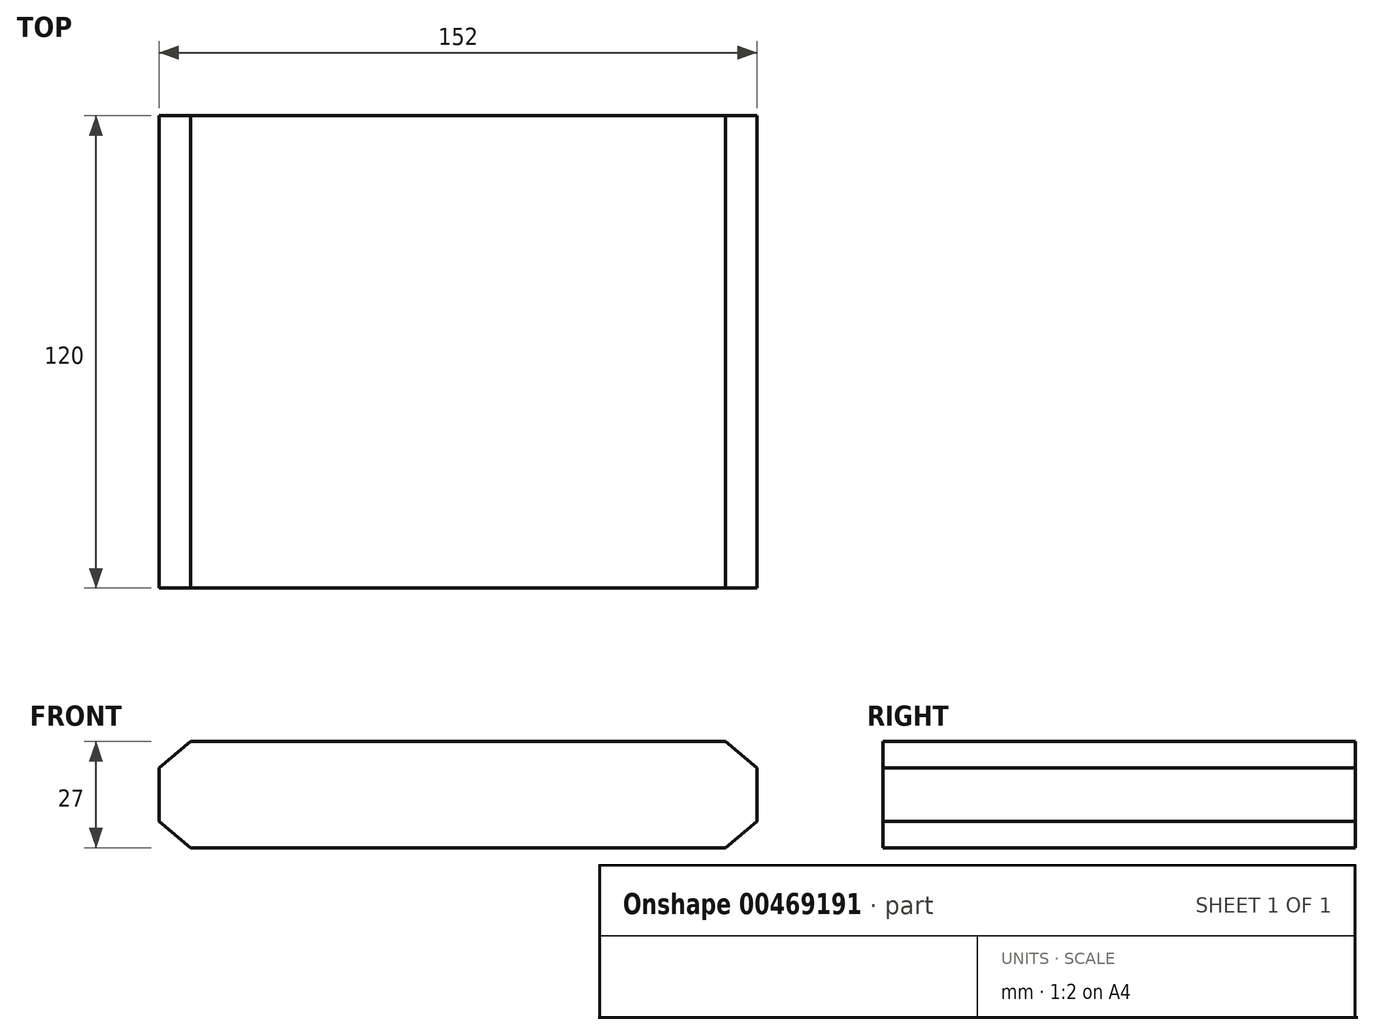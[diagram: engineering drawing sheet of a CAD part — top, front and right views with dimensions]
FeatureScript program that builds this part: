
annotation { "Feature Type Name" : "Feature", "Feature Type Description" : "" }
export const myFeature = defineFeature(function(context is Context, id is Id, definition is map)
    precondition{}
    {
        {
            var Q0;
            Q0=qCreatedBy(makeId("Top.planeOp"),FACE);
            var sketch = newSketch(context, id + "F0", { "sketchPlane" : qUnion([Q0])});
            skLineSegment(sketch, "E0.bottom", {"start": v(76, -60) * mm, "end": v(-76, -60) * mm});
            skLineSegment(sketch, "E0.top", {"start": v(76, 60) * mm, "end": v(-76, 60) * mm});
            skLineSegment(sketch, "E0.left", {"start": v(76, -60) * mm, "end": v(76, 60) * mm});
            skLineSegment(sketch, "E0.right", {"start": v(-76, -60) * mm, "end": v(-76, 60) * mm});
            skPoint(sketch, "E0.middle", {"position": v(0, 0) * mm});
            skSolve(sketch);
        }
        {
            var Q0;
            Q0 = qSketchRegion(id + "F0", true);
            extrude(context, id + "F1", {"entities" : qUnion([Q0]), "depth" : 27 * mm});
        }
        {
            var Q0;
            Q0=makeQuery(id+"F1.opExtrude","SWEPT_FACE",FACE,{"disambiguationData":[OSD([sQuery(id+"F0.wireOp",EDGE,"E0.top")])]});
            var sketch = newSketch(context, id + "F2", { "sketchPlane" : qUnion([Q0])});
            skLineSegment(sketch, "E1.bottom", {"start": v(60, 0) * mm, "end": v(-60, 0) * mm});
            skLineSegment(sketch, "E1.top", {"start": v(60, 27) * mm, "end": v(-60, 27) * mm});
            skLineSegment(sketch, "E1.left", {"start": v(60, 0) * mm, "end": v(60, 27) * mm});
            skLineSegment(sketch, "E1.right", {"start": v(-60, 0) * mm, "end": v(-60, 27) * mm});
            skPoint(sketch, "E1.middle", {"position": v(0, 13.5) * mm});
            skPoint(sketch, "E1.middle.positionSnap0", {"position": v(76, 13.5) * mm});
            skPoint(sketch, "E1.centerSnap0", {"position": v(76, 13.5) * mm});
            skLineSegment(sketch, "E2", {"start": v(-60, 27) * mm, "end": v(-76, 27) * mm});
            skLineSegment(sketch, "E3", {"start": v(-76, 27) * mm, "end": v(-76, 0) * mm});
            skLineSegment(sketch, "E4", {"start": v(-76, 0) * mm, "end": v(-60, 0) * mm});
            skLineSegment(sketch, "E5", {"start": v(60, 0) * mm, "end": v(76, 0) * mm});
            skLineSegment(sketch, "E6", {"start": v(76, 0) * mm, "end": v(76, 27) * mm});
            skLineSegment(sketch, "E7", {"start": v(76, 27) * mm, "end": v(60, 27) * mm});
            skLineSegment(sketch, "E8", {"start": v(76, 13.5) * mm, "end": v(76, 27) * mm});
            skLineSegment(sketch, "E9", {"start": v(76, 13.5) * mm, "end": v(76, 0) * mm});
            skLineSegment(sketch, "E10", {"start": v(-76, 13.5) * mm, "end": v(-76, 27) * mm});
            skLineSegment(sketch, "E11", {"start": v(-76, 13.5) * mm, "end": v(-76, 0) * mm});
            skLineSegment(sketch, "E12", {"start": v(-76, 6.75) * mm, "end": v(-68, 0) * mm});
            skLineSegment(sketch, "E13", {"start": v(-76, 20.25) * mm, "end": v(-68, 27) * mm});
            skLineSegment(sketch, "E14", {"start": v(68, 27) * mm, "end": v(76, 20.25) * mm});
            skLineSegment(sketch, "E15", {"start": v(68, 0) * mm, "end": v(76, 6.75) * mm});
            skSolve(sketch);
        }
        {
            var Q0;
            {var subQ3=sQuery(id+"F2.wireOp",EDGE,"E13");Q0=makeQuery(id+"F2.imprint","IMPRINT",FACE,{"disambiguationData":[TD([[makeQuery(id+"F2.imprint","IMPRINT",EDGE,{"derivedFrom":subQ3}),1.0]])]});}
            var Q1;
            {var subQ3=sQuery(id+"F2.wireOp",EDGE,"E12");Q1=makeQuery(id+"F2.imprint","IMPRINT",FACE,{"disambiguationData":[TD([[makeQuery(id+"F2.imprint","IMPRINT",EDGE,{"derivedFrom":subQ3}),-1.0]])]});}
            var Q2;
            {var subQ3=sQuery(id+"F2.wireOp",EDGE,"E15");Q2=makeQuery(id+"F2.imprint","IMPRINT",FACE,{"disambiguationData":[TD([[makeQuery(id+"F2.imprint","IMPRINT",EDGE,{"derivedFrom":subQ3}),-1.0]])]});}
            var Q3;
            {var subQ3=sQuery(id+"F2.wireOp",EDGE,"E14");Q3=makeQuery(id+"F2.imprint","IMPRINT",FACE,{"disambiguationData":[TD([[makeQuery(id+"F2.imprint","IMPRINT",EDGE,{"derivedFrom":subQ3}),1.0]])]});}
            extrude(context, id + "F3", {"entities" : qUnion([Q0, Q1, Q2, Q3]), "operationType" : NewBodyOperationType.REMOVE, "endBound" : BoundingType.THROUGH_ALL, "oppositeDirection" : true, "depth" : 25 * mm});
        }
    });
